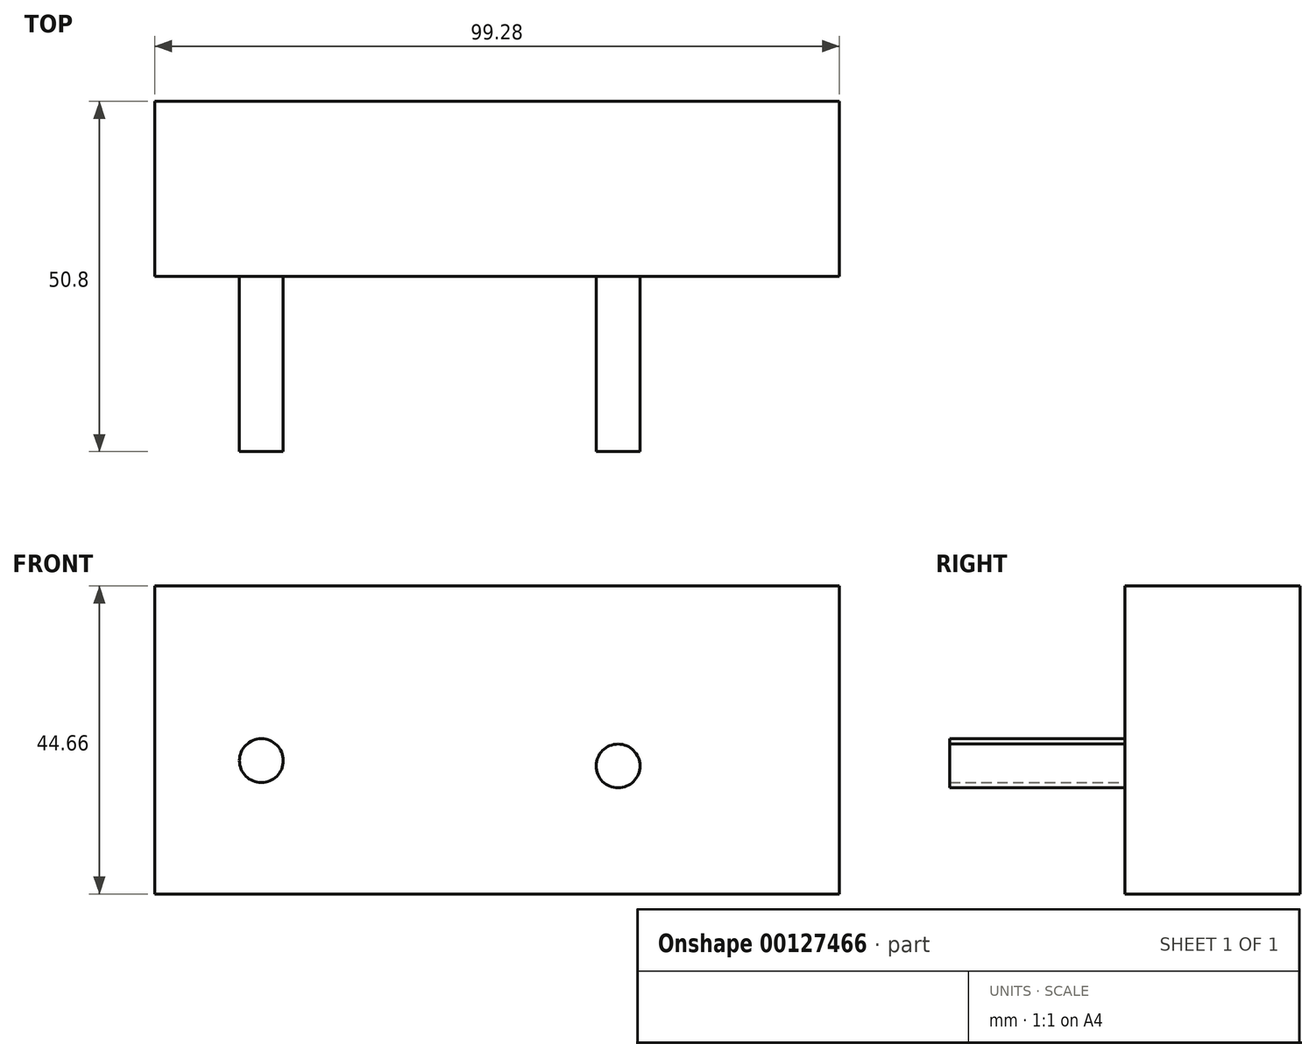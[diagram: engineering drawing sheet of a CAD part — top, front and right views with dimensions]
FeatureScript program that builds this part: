
annotation { "Feature Type Name" : "Feature", "Feature Type Description" : "" }
export const myFeature = defineFeature(function(context is Context, id is Id, definition is map)
    precondition{}
    {
        {
            var Q0;
            Q0=qCreatedBy(makeId("Front.planeOp"),FACE);
            var sketch = newSketch(context, id + "F0", { "sketchPlane" : qUnion([Q0])});
            skLineSegment(sketch, "E0.bottom", {"start": v(-45.3, 21.8) * mm, "end": v(53.98, 21.8) * mm});
            skLineSegment(sketch, "E0.top", {"start": v(-45.3, -22.86) * mm, "end": v(53.98, -22.86) * mm});
            skLineSegment(sketch, "E0.left", {"start": v(-45.3, 21.8) * mm, "end": v(-45.3, -22.86) * mm});
            skLineSegment(sketch, "E0.right", {"start": v(53.98, 21.8) * mm, "end": v(53.98, -22.86) * mm});
            skSolve(sketch);
        }
        {
            var Q0;
            Q0=makeQuery(id+"F0.imprint","IMPRINT",FACE,{"disambiguationData":[TD([[makeQuery(id+"F0.imprint","IMPRINT",EDGE,{"derivedFrom":sQuery(id+"F0.wireOp",EDGE,"E0.bottom")}),-1.0]])]});
            extrude(context, id + "F1", {"entities" : qUnion([Q0]), "depth" : 25.4 * mm});
        }
        {
            var Q0;
            Q0=makeQuery(id+"F1.opExtrude","CAP_FACE",FACE,{"disambiguationData":[OSD([sQuery(id+"F0.wireOp",EDGE,"E0.bottom"),sQuery(id+"F0.wireOp",EDGE,"E0.top"),sQuery(id+"F0.wireOp",EDGE,"E0.left"),sQuery(id+"F0.wireOp",EDGE,"E0.right")])],"isStart":false});
            var sketch = newSketch(context, id + "F2", { "sketchPlane" : qUnion([Q0])});
            skCircle(sketch, "E1", {"center": v(-29.81, -3.53) * mm, "radius": 3.18 * mm});
            skCircle(sketch, "E2", {"center": v(21.9, -4.3) * mm, "radius": 3.18 * mm});
            skSolve(sketch);
        }
        {
            var Q0;
            Q0=qSketchRegion(id+"F2",true);
            extrude(context, id + "F3", {"entities" : qUnion([Q0]), "operationType" : NewBodyOperationType.ADD, "depth" : 25.4 * mm});
        }
    });
